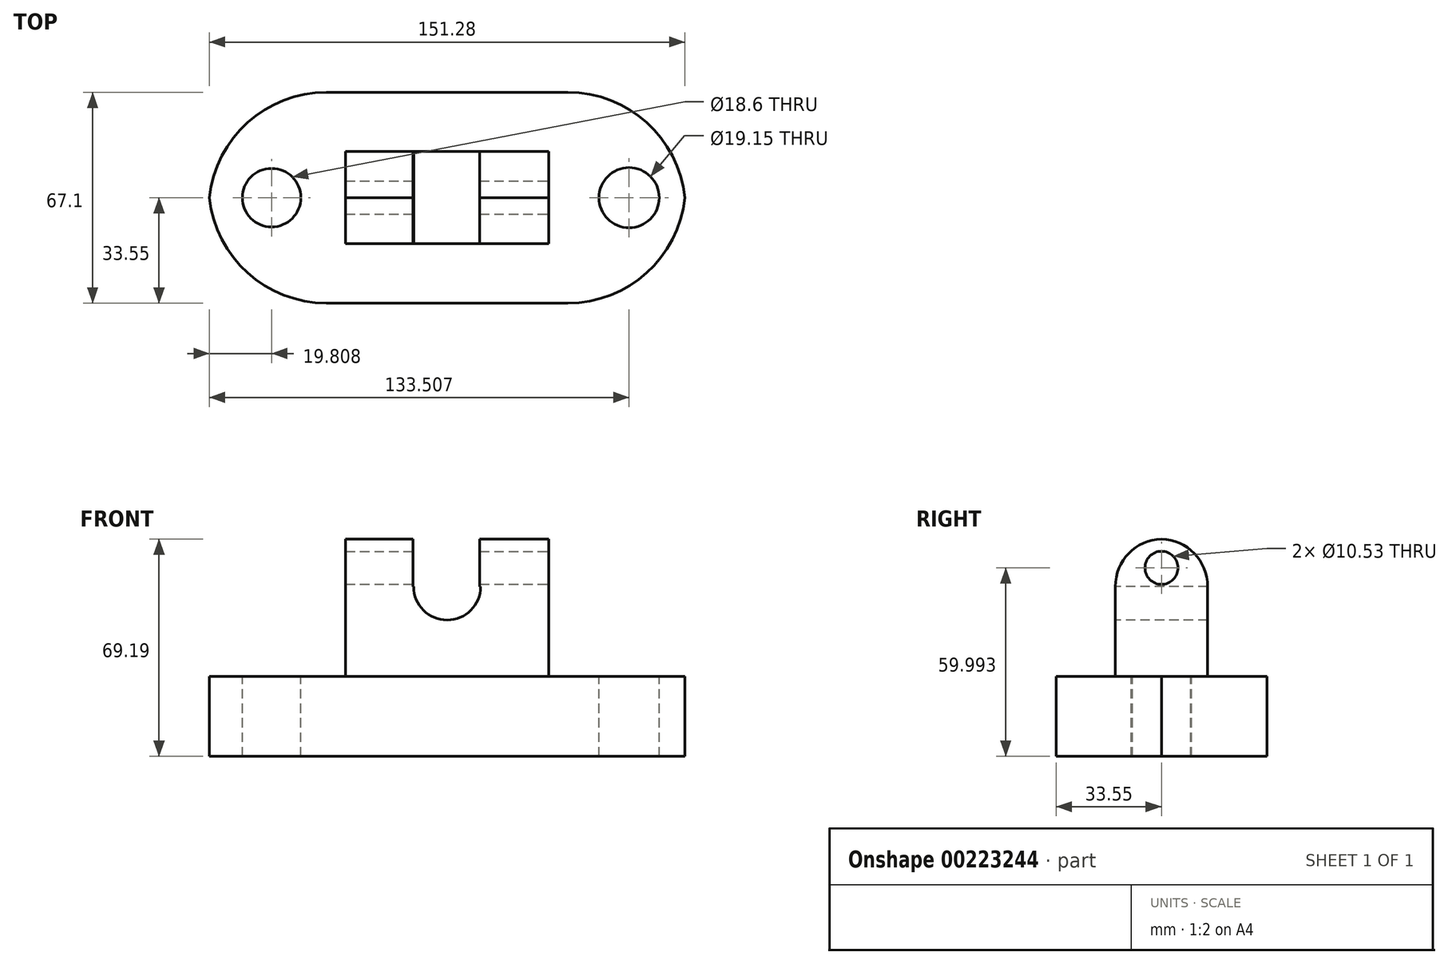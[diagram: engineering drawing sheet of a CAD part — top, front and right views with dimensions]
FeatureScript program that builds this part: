
annotation { "Feature Type Name" : "Feature", "Feature Type Description" : "" }
export const myFeature = defineFeature(function(context is Context, id is Id, definition is map)
    precondition{}
    {
        {
            var Q0;
            Q0=qCreatedBy(makeId("Top.planeOp"),FACE);
            var sketch = newSketch(context, id + "F0", { "sketchPlane" : qUnion([Q0])});
            skLineSegment(sketch, "E0.bottom", {"start": v(75.84, 33.55) * mm, "end": v(-75.84, 33.55) * mm});
            skLineSegment(sketch, "E0.top", {"start": v(75.84, -33.55) * mm, "end": v(-75.84, -33.55) * mm});
            skLineSegment(sketch, "E0.left", {"start": v(75.84, 33.55) * mm, "end": v(75.84, -33.55) * mm});
            skLineSegment(sketch, "E0.right", {"start": v(-75.84, 33.55) * mm, "end": v(-75.84, -33.55) * mm});
            skPoint(sketch, "E0.middle", {"position": v(0, 0) * mm});
            skSolve(sketch);
        }
        {
            var Q0;
            Q0=makeQuery(id+"F0.imprint","IMPRINT",FACE,{"disambiguationData":[TD([[makeQuery(id+"F0.imprint","IMPRINT",EDGE,{"derivedFrom":sQuery(id+"F0.wireOp",EDGE,"E0.bottom")}),1.0]])]});
            extrude(context, id + "F1", {"entities" : qUnion([Q0]), "depth" : 25.4 * mm});
        }
        {
            var Q0;
            Q0=makeQuery(id+"F1.opExtrude","SWEPT_EDGE",EDGE,{"disambiguationData":[OSD([sQuery(id+"F0.wireOp",EDGE,"E0.bottom"),sQuery(id+"F0.wireOp",EDGE,"E0.left")])]});
            var Q1;
            Q1=makeQuery(id+"F1.opExtrude","SWEPT_EDGE",EDGE,{"disambiguationData":[OSD([sQuery(id+"F0.wireOp",EDGE,"E0.top"),sQuery(id+"F0.wireOp",EDGE,"E0.left")])]});
            var Q2;
            Q2=makeQuery(id+"F1.opExtrude","SWEPT_EDGE",EDGE,{"disambiguationData":[OSD([sQuery(id+"F0.wireOp",EDGE,"E0.top"),sQuery(id+"F0.wireOp",EDGE,"E0.right")])]});
            var Q3;
            Q3=makeQuery(id+"F1.opExtrude","SWEPT_EDGE",EDGE,{"disambiguationData":[OSD([sQuery(id+"F0.wireOp",EDGE,"E0.bottom"),sQuery(id+"F0.wireOp",EDGE,"E0.right")])]});
            fillet(context, id + "F9", {"entities" : qUnion([Q0, Q1, Q2, Q3]), "radius" : 37.47 * mm, "tangentPropagation" : true, "allowEdgeOverflow" : false});
        }
        {
            var Q0;
            Q0=makeQuery(id+"F1.opExtrude","CAP_FACE",FACE,{"disambiguationData":[OSD([sQuery(id+"F0.wireOp",EDGE,"E0.bottom"),sQuery(id+"F0.wireOp",EDGE,"E0.top"),sQuery(id+"F0.wireOp",EDGE,"E0.left"),sQuery(id+"F0.wireOp",EDGE,"E0.right")])],"isStart":false});
            var sketch = newSketch(context, id + "F2", { "sketchPlane" : qUnion([Q0])});
            skCircle(sketch, "E1", {"center": v(-55.83, 0) * mm, "radius": 9.3 * mm});
            skCircle(sketch, "E2", {"center": v(57.87, 0) * mm, "radius": 9.57 * mm});
            skSolve(sketch);
        }
        {
            var Q0;
            Q0=makeQuery(id+"F2.imprint","IMPRINT",FACE,{"disambiguationData":[TD([[makeQuery(id+"F2.imprint","IMPRINT",EDGE,{"derivedFrom":sQuery(id+"F2.wireOp",EDGE,"E2")}),1.0]])]});
            var Q1;
            Q1=makeQuery(id+"F2.imprint","IMPRINT",FACE,{"disambiguationData":[TD([[makeQuery(id+"F2.imprint","IMPRINT",EDGE,{"derivedFrom":sQuery(id+"F2.wireOp",EDGE,"E1")}),1.0]])]});
            extrude(context, id + "F3", {"entities" : qUnion([Q0, Q1]), "operationType" : NewBodyOperationType.REMOVE, "endBound" : BoundingType.THROUGH_ALL, "oppositeDirection" : true, "depth" : 25.4 * mm});
        }
        {
            var Q0;
            Q0=makeQuery(id+"F1.opExtrude","CAP_FACE",FACE,{"disambiguationData":[OSD([sQuery(id+"F0.wireOp",EDGE,"E0.bottom"),sQuery(id+"F0.wireOp",EDGE,"E0.top"),sQuery(id+"F0.wireOp",EDGE,"E0.left"),sQuery(id+"F0.wireOp",EDGE,"E0.right")])],"isStart":false});
            var sketch = newSketch(context, id + "F4", { "sketchPlane" : qUnion([Q0])});
            skLineSegment(sketch, "E3.bottom", {"start": v(32.3, -14.66) * mm, "end": v(-32.3, -14.66) * mm});
            skLineSegment(sketch, "E3.top", {"start": v(32.3, 14.66) * mm, "end": v(-32.3, 14.66) * mm});
            skLineSegment(sketch, "E3.left", {"start": v(32.3, -14.66) * mm, "end": v(32.3, 14.66) * mm});
            skLineSegment(sketch, "E3.right", {"start": v(-32.3, -14.66) * mm, "end": v(-32.3, 14.66) * mm});
            skPoint(sketch, "E3.middle", {"position": v(0, 0) * mm});
            skSolve(sketch);
        }
        {
            var Q0;
            Q0=makeQuery(id+"F4.imprint","IMPRINT",FACE,{"disambiguationData":[TD([[makeQuery(id+"F4.imprint","IMPRINT",EDGE,{"derivedFrom":sQuery(id+"F4.wireOp",EDGE,"E3.bottom")}),-1.0]])]});
            extrude(context, id + "F10", {"entities" : qUnion([Q0]), "operationType" : NewBodyOperationType.ADD, "depth" : 43.8 * mm});
        }
        {
            var Q0;
            Q0=makeQuery(id+"F10.opExtrude","CAP_EDGE",EDGE,{"disambiguationData":[OSD([sQuery(id+"F4.wireOp",EDGE,"E3.bottom")])],"isStart":false});
            var Q1;
            Q1=makeQuery(id+"F10.opExtrude","CAP_EDGE",EDGE,{"disambiguationData":[OSD([sQuery(id+"F4.wireOp",EDGE,"E3.top")])],"isStart":false});
            fillet(context, id + "F11", {"entities" : qUnion([Q0, Q1]), "radius" : 15.17 * mm, "tangentPropagation" : true, "allowEdgeOverflow" : false});
        }
        {
            var Q0;
            Q0=makeQuery(id+"F10.opExtrude","SWEPT_FACE",FACE,{"disambiguationData":[OSD([sQuery(id+"F4.wireOp",EDGE,"E3.left")])]});
            var sketch = newSketch(context, id + "F5", { "sketchPlane" : qUnion([Q0])});
            skCircle(sketch, "E4", {"center": v(0, 60) * mm, "radius": 5.26 * mm});
            skSolve(sketch);
        }
        {
            var Q0;
            Q0=makeQuery(id+"F5.imprint","IMPRINT",FACE,{"disambiguationData":[TD([[makeQuery(id+"F5.imprint","IMPRINT",EDGE,{"derivedFrom":sQuery(id+"F5.wireOp",EDGE,"E4")}),1.0]])]});
            extrude(context, id + "F6", {"entities" : qUnion([Q0]), "operationType" : NewBodyOperationType.REMOVE, "endBound" : BoundingType.THROUGH_ALL, "oppositeDirection" : true, "depth" : 25.4 * mm});
        }
        {
            var Q0;
            Q0=makeQuery(id+"F10.opExtrude","SWEPT_FACE",FACE,{"disambiguationData":[OSD([sQuery(id+"F4.wireOp",EDGE,"E3.bottom")])]});
            var sketch = newSketch(context, id + "F7", { "sketchPlane" : qUnion([Q0])});
            skLineSegment(sketch, "E5.bottom", {"start": v(-10.84, 54.03) * mm, "end": v(10.4, 54.03) * mm});
            skLineSegment(sketch, "E5.top", {"start": v(-10.84, 74.84) * mm, "end": v(10.4, 74.84) * mm});
            skLineSegment(sketch, "E5.left", {"start": v(-10.84, 54.03) * mm, "end": v(-10.84, 74.84) * mm});
            skLineSegment(sketch, "E5.right", {"start": v(10.4, 54.03) * mm, "end": v(10.4, 74.84) * mm});
            skCircle(sketch, "E6", {"center": v(0, 54.03) * mm, "radius": 10.65 * mm});
            skSolve(sketch);
        }
        {
            var Q0;
            {var subQ1=sQuery(id+"F7.wireOp",EDGE,"E5.top");Q0=makeQuery(id+"F7.imprint","IMPRINT",FACE,{"disambiguationData":[TD([[makeQuery(id+"F7.imprint","IMPRINT",EDGE,{"derivedFrom":subQ1}),-1.0]])]});}
            var Q1;
            {var subQ0=sQuery(id+"F7.wireOp",EDGE,"E5.right");var subQ4=sQuery(id+"F7.wireOp",EDGE,"E6");var subQ6=makeQuery(id+"F7.imprint","INTERSECT",VERTEX,{"derivedFrom":[subQ0,subQ4]});Q1=makeQuery(id+"F7.imprint","IMPRINT",FACE,{"disambiguationData":[TD([[makeQuery(id+"F7.imprint","IMPRINT",EDGE,{"disambiguationData":[TD([[subQ6,-1.0]])],"derivedFrom":subQ4}),1.0]])]});}
            var Q2;
            {var subQ0=sQuery(id+"F7.wireOp",EDGE,"E5.bottom");var subQ4=sQuery(id+"F7.wireOp",EDGE,"E6");var subQ5=makeQuery(id+"F7.imprint","INTERSECT",VERTEX,{"derivedFrom":[subQ0,subQ4]});Q2=makeQuery(id+"F7.imprint","IMPRINT",FACE,{"disambiguationData":[TD([[makeQuery(id+"F7.imprint","IMPRINT",EDGE,{"disambiguationData":[TD([[subQ5,-1.0]])],"derivedFrom":subQ4}),1.0]])]});}
            extrude(context, id + "F8", {"entities" : qUnion([Q0, Q1, Q2]), "operationType" : NewBodyOperationType.REMOVE, "endBound" : BoundingType.THROUGH_ALL, "oppositeDirection" : true, "depth" : 25.4 * mm});
        }
    });
